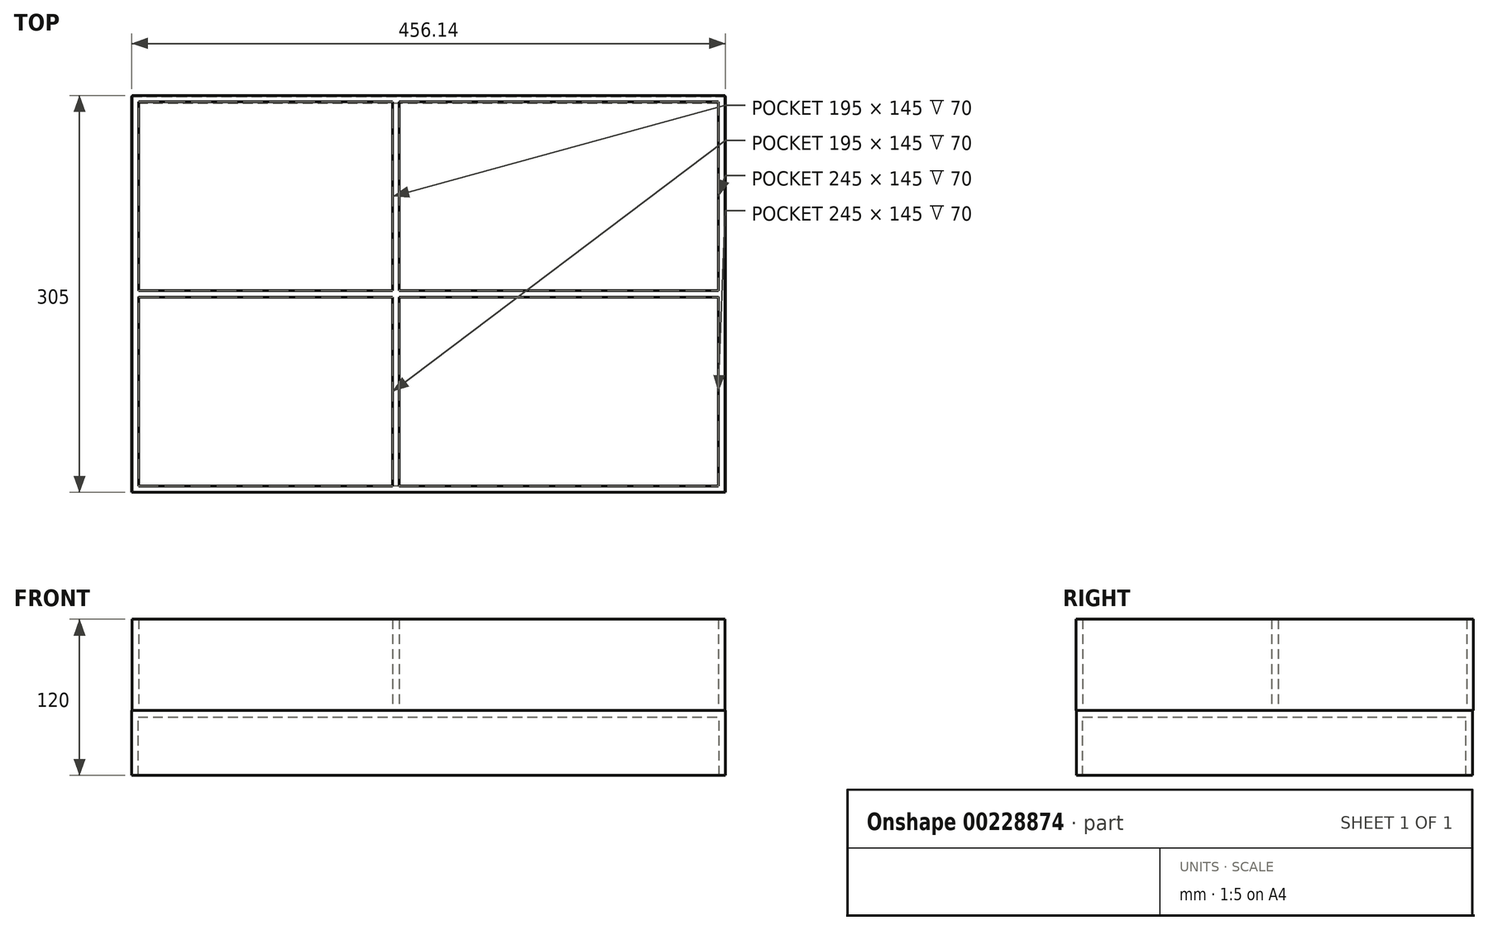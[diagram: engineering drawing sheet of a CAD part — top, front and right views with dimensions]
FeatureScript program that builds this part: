
annotation { "Feature Type Name" : "Feature", "Feature Type Description" : "" }
export const myFeature = defineFeature(function(context is Context, id is Id, definition is map)
    precondition{}
    {
        {
            var Q0;
            Q0=qCreatedBy(makeId("Top.planeOp"),FACE);
            var sketch = newSketch(context, id + "F0", { "sketchPlane" : qUnion([Q0])});
            skLineSegment(sketch, "E0.bottom", {"start": v(-229.98, 150) * mm, "end": v(225.02, 150) * mm});
            skLineSegment(sketch, "E0.top", {"start": v(-229.98, -155) * mm, "end": v(225.02, -155) * mm});
            skLineSegment(sketch, "E0.left", {"start": v(-229.98, 150) * mm, "end": v(-229.98, -155) * mm});
            skLineSegment(sketch, "E0.right", {"start": v(225.02, 150) * mm, "end": v(225.02, -155) * mm});
            skLineSegment(sketch, "E1.bottom", {"start": v(-224.98, 145) * mm, "end": v(-29.98, 145) * mm});
            skLineSegment(sketch, "E1.top", {"start": v(-224.98, 0) * mm, "end": v(-29.98, 0) * mm});
            skLineSegment(sketch, "E1.left", {"start": v(-224.98, 145) * mm, "end": v(-224.98, 0) * mm});
            skLineSegment(sketch, "E1.right", {"start": v(-29.98, 145) * mm, "end": v(-29.98, 0) * mm});
            skLineSegment(sketch, "E2.0.1.0", {"start": v(-224.98, -5) * mm, "end": v(-224.98, -150) * mm});
            skLineSegment(sketch, "E2.0.1.1", {"start": v(-224.98, -150) * mm, "end": v(-29.98, -150) * mm});
            skLineSegment(sketch, "E2.0.1.2", {"start": v(-29.98, -5) * mm, "end": v(-29.98, -150) * mm});
            skLineSegment(sketch, "E2.0.1.3", {"start": v(-224.98, -5) * mm, "end": v(-29.98, -5) * mm});
            skLineSegment(sketch, "E2.direction1", {"start": v(-224.98, 0) * mm, "end": v(-199.98, 0) * mm, "construction": true});
            skLineSegment(sketch, "E2.direction2", {"start": v(-224.98, 0) * mm, "end": v(-224.98, -150) * mm, "construction": true});
            skLineSegment(sketch, "E3.bottom", {"start": v(-24.98, 145) * mm, "end": v(220.02, 145) * mm});
            skLineSegment(sketch, "E3.top", {"start": v(-24.98, 0) * mm, "end": v(220.02, 0) * mm});
            skLineSegment(sketch, "E3.left", {"start": v(-24.98, 145) * mm, "end": v(-24.98, 0) * mm});
            skLineSegment(sketch, "E3.right", {"start": v(220.02, 145) * mm, "end": v(220.02, 0) * mm});
            skLineSegment(sketch, "E4.0.1.0", {"start": v(-24.98, -5) * mm, "end": v(-24.98, -150) * mm});
            skLineSegment(sketch, "E4.0.1.1", {"start": v(-24.98, -150) * mm, "end": v(220.02, -150) * mm});
            skLineSegment(sketch, "E4.0.1.2", {"start": v(220.02, -5) * mm, "end": v(220.02, -150) * mm});
            skLineSegment(sketch, "E4.0.1.3", {"start": v(-24.98, -5) * mm, "end": v(220.02, -5) * mm});
            skLineSegment(sketch, "E4.direction1", {"start": v(-24.98, 0) * mm, "end": v(0.02, 0) * mm, "construction": true});
            skLineSegment(sketch, "E4.direction2", {"start": v(-24.98, 0) * mm, "end": v(-24.98, -150) * mm, "construction": true});
            skSolve(sketch);
        }
        {
            var Q0;
            Q0 = qSketchRegion(id + "F0", true);
            extrude(context, id + "F1", {"entities" : qUnion([Q0]), "depth" : 70 * mm});
        }
        {
            var Q0;
            Q0=makeQuery(id+"F0.imprint","IMPRINT",FACE,{"disambiguationData":[TD([[makeQuery(id+"F0.imprint","IMPRINT",EDGE,{"derivedFrom":sQuery(id+"F0.wireOp",EDGE,"E2.0.1.0")}),1.0]])]});
            var sketch = newSketch(context, id + "F2", { "sketchPlane" : qUnion([Q0])});
            skLineSegment(sketch, "E5.bottom", {"start": v(-230.51, -154.91) * mm, "end": v(225.63, -154.91) * mm});
            skLineSegment(sketch, "E5.top", {"start": v(-230.51, 149.26) * mm, "end": v(225.63, 149.26) * mm});
            skLineSegment(sketch, "E5.left", {"start": v(-230.51, -154.91) * mm, "end": v(-230.51, 149.26) * mm});
            skLineSegment(sketch, "E5.right", {"start": v(225.63, -154.91) * mm, "end": v(225.63, 149.26) * mm});
            skSolve(sketch);
        }
        {
            var Q0;
            Q0 = qSketchRegion(id + "F2", true);
            extrude(context, id + "F3", {"entities" : qUnion([Q0]), "operationType" : NewBodyOperationType.ADD, "oppositeDirection" : true, "depth" : 5 * mm});
        }
        {
            var Q0;
            Q0=makeQuery(id+"F3.opExtrude","CAP_FACE",FACE,{"disambiguationData":[OSD([sQuery(id+"F2.wireOp",EDGE,"E5.bottom"),sQuery(id+"F2.wireOp",EDGE,"E5.top"),sQuery(id+"F2.wireOp",EDGE,"E5.left"),sQuery(id+"F2.wireOp",EDGE,"E5.right")])],"isStart":false});
            var sketch = newSketch(context, id + "F4", { "sketchPlane" : qUnion([Q0])});
            skLineSegment(sketch, "E6.bottom", {"start": v(-225.51, 149.91) * mm, "end": v(220.63, 149.91) * mm});
            skLineSegment(sketch, "E6.top", {"start": v(-225.51, -144.26) * mm, "end": v(220.63, -144.26) * mm});
            skLineSegment(sketch, "E6.left", {"start": v(-225.51, 149.91) * mm, "end": v(-225.51, -144.26) * mm});
            skLineSegment(sketch, "E6.right", {"start": v(220.63, 149.91) * mm, "end": v(220.63, -144.26) * mm});
            skSolve(sketch);
        }
        {
            var Q0;
            Q0=makeQuery(id+"F4.imprint","IMPRINT",FACE,{"disambiguationData":[TD([[makeQuery(id+"F4.imprint","IMPRINT",EDGE,{"derivedFrom":sQuery(id+"F4.wireOp",EDGE,"E6.bottom")}),1.0]])]});
            extrude(context, id + "F5", {"entities" : qUnion([Q0]), "operationType" : NewBodyOperationType.ADD, "depth" : 45 * mm});
        }
    });
